# Revit family: EGCODORNWN210_z55
name_source: partatom
category: Allgemeines Modell
units: mm (PartAtom-declared; Revit-internal decimal feet)

## family parameters
Arbeitsebenenbasiert = Nein
Beim Laden mit Abzugskörper schneiden = Nein
Bemaßung runder Anschluss = Durchmesser verwenden
Beschriftungsausrichtung beibehalten = Nein
Gemeinsam genutzt = Nein
Immer vertikal = Ja
Kann Basisbauteil für Bewehrung sein = Nein
Raumberechnungspunkt = Nein
Teiletyp = Normal

## types (1)
- EGCODORNWN210_z55
    Bauteilnummer = EGCODORNWN210
    DocNumber = EGCODORNWN%.iam
    Erstellungsdatum = 22.04.2021
    Folder = ARTIKEL\G3_Bewehrungstechnik\G3C_Dornsysteme\Egcodorn\
    Genehmigungsdatum Konstr. = 24.01.2025
    Gewicht = 3.029
    Kennung = Artikel
    Konstruktionsstatus = 1
    Revisionsnummer = -
    Status = In Korrektur
    Typ = 210 mm  [stored 0.688976 ft]
    VDS_Category = iAssembly Familie
    Vorgabe-Ansicht = 0 mm  [stored 0 ft]

note: [stored X ft] marks values corroborated as IEEE doubles in the binary element streams (Revit-internal decimal feet)
